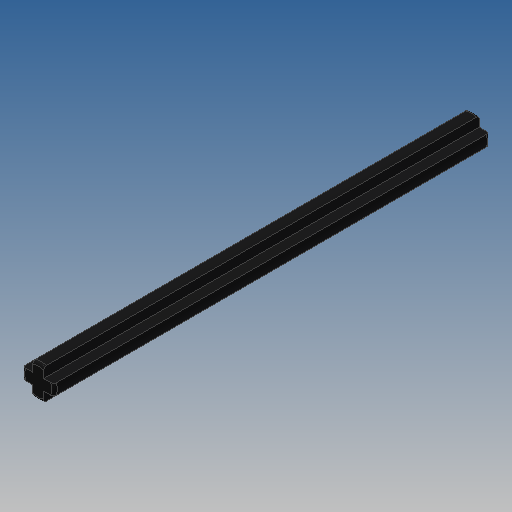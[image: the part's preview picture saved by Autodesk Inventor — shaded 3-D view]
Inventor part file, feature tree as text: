
AUTODESK INVENTOR PART (.ipt)
format: ipt  version: 2022.2 (Build 262287000, 287)  size: 138,752 bytes
history: native  units: in
note: dims shown in document units (in); Inventor stores cm internally (conversion verified against a paired STEP export)
features: extrude x1, fillet x1, sketch x1
ambient origin geometry x8: Origin, YZ Plane, XZ Plane, XY Plane, X Axis, Y Axis, Z Axis, Center Point
bodies: Solid1 (feature_tree)
feature tree (3):
  extrude  "Extrusion1"  Depth=0.0157in
  fillet  "Fillet1"  Radius=2.5197in
  sketch  "Sketch1"  dims[d0=0.189in d1=0.063in d2=2.5197in d3=0.0in d4=0.0157in d5=0.0in d6=0.0in]
